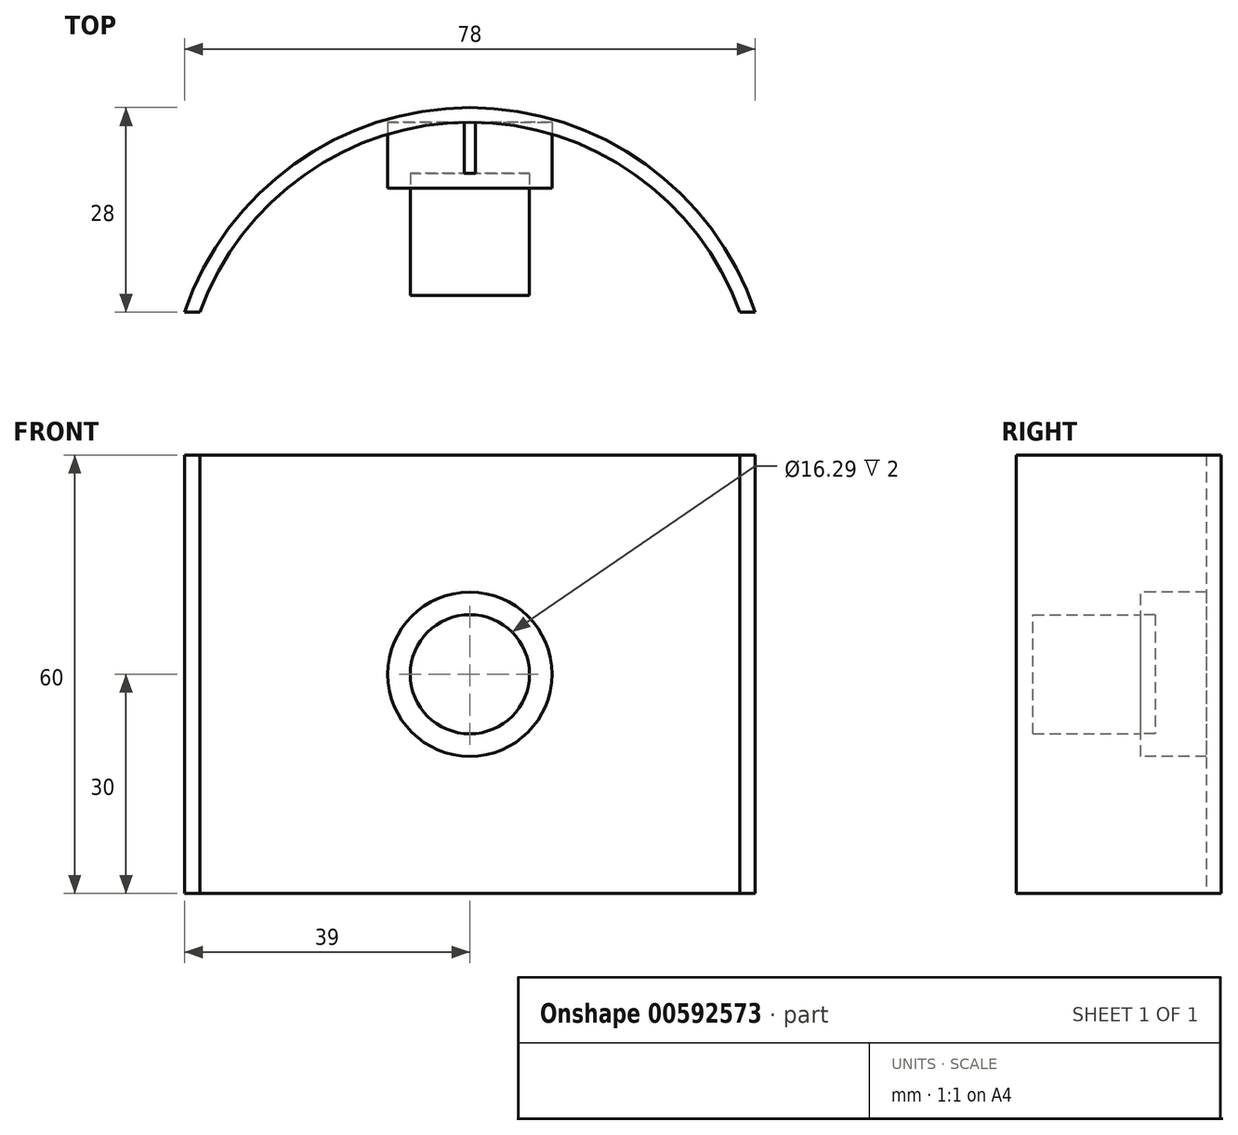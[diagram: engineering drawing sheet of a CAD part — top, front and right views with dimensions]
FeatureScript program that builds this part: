
annotation { "Feature Type Name" : "Feature", "Feature Type Description" : "" }
export const myFeature = defineFeature(function(context is Context, id is Id, definition is map)
    precondition{}
    {
        {
            assignVariable(context, id + "F0", {"name" : "shaft_H1", "anyValue" : 14.7 * mm});
        }
        {
            assignVariable(context, id + "F1", {"name" : "Shaft_H2", "anyValue" : 23.7 * mm});
        }
        {
            assignVariable(context, id + "F2", {"name" : "support", "anyValue" : 16.7 * mm});
        }
        {
            assignVariable(context, id + "F3", {"name" : "HUB_depth1", "anyValue" : getVariable(context, 'support') - getVariable(context, 'shaft_H1')});
        }
        {
            assignVariable(context, id + "F4", {"name" : "support_H1", "anyValue" : getVariable(context, 'Shaft_H2') - getVariable(context, 'shaft_H1') - getVariable(context, 'HUB_depth1')});
        }
        {
            var Q0;
            Q0=qCreatedBy(makeId("Front.planeOp"),FACE);
            var sketch = newSketch(context, id + "F5", { "sketchPlane" : qUnion([Q0])});
            skCircle(sketch, "E0", {"center": v(0, 0) * mm, "radius": 26.88 * mm});
            skCircle(sketch, "E1", {"center": v(0, 0) * mm, "radius": 8.15 * mm, "construction": true});
            skCircle(sketch, "E2", {"center": v(0, 0) * mm, "radius": 11.23 * mm, "construction": true});
            skLineSegment(sketch, "E3", {"start": v(-26.88, 0) * mm, "end": v(26.88, 0) * mm, "construction": true});
            skLineSegment(sketch, "E4", {"start": v(0, -26.88) * mm, "end": v(0, 26.88) * mm, "construction": true});
            skLineSegment(sketch, "E5", {"start": v(0, 26.88) * mm, "end": v(19, 19) * mm, "construction": true});
            skLineSegment(sketch, "E6", {"start": v(19, 19) * mm, "end": v(26.88, 0) * mm, "construction": true});
            skLineSegment(sketch, "E7", {"start": v(26.87, 0) * mm, "end": v(19, -19) * mm, "construction": true});
            skLineSegment(sketch, "E8", {"start": v(19, -19) * mm, "end": v(0, -26.88) * mm, "construction": true});
            skLineSegment(sketch, "E9", {"start": v(0, -26.88) * mm, "end": v(-19, -19) * mm, "construction": true});
            skLineSegment(sketch, "E10", {"start": v(-19, -19) * mm, "end": v(-26.87, 0) * mm, "construction": true});
            skLineSegment(sketch, "E11", {"start": v(-26.88, 0) * mm, "end": v(-19, 19) * mm, "construction": true});
            skLineSegment(sketch, "E12", {"start": v(-19, 19) * mm, "end": v(0, 26.88) * mm, "construction": true});
            skLineSegment(sketch, "E13", {"start": v(-19, 19) * mm, "end": v(19, -19) * mm, "construction": true});
            skLineSegment(sketch, "E14", {"start": v(19, 19) * mm, "end": v(-19, -19) * mm, "construction": true});
            skCircle(sketch, "E15.0", {"center": v(0, 0) * mm, "radius": 28.38 * mm});
            skLineSegment(sketch, "E16", {"start": v(0, -30) * mm, "end": v(0, 30) * mm, "construction": true});
            skLineSegment(sketch, "E17", {"start": v(39, 0) * mm, "end": v(-39, 0) * mm, "construction": true});
            skSolve(sketch);
        }
        {
            var Q0;
            Q0=qCreatedBy(makeId("Front.planeOp"),FACE);
            var sketch = newSketch(context, id + "F6", { "sketchPlane" : qUnion([Q0])});
            skCircle(sketch, "E18", {"center": v(0, 0) * mm, "radius": 8.15 * mm});
            skCircle(sketch, "E19", {"center": v(0, 0) * mm, "radius": 11.23 * mm});
            skSolve(sketch);
        }
        {
            var Q0;
            Q0=makeQuery(id+"F6.imprint","IMPRINT",FACE,{"disambiguationData":[TD([[makeQuery(id+"F6.imprint","IMPRINT",EDGE,{"derivedFrom":sQuery(id+"F6.wireOp",EDGE,"E18")}),1.0]])]});
            extrude(context, id + "F7", {"entities" : qUnion([Q0]), "depth" : getVariable(context, 'shaft_H1'), "offsetDistance" : 25.4 * mm});
        }
        {
            var Q0;
            Q0=makeQuery(id+"F6.imprint","IMPRINT",FACE,{"disambiguationData":[TD([[makeQuery(id+"F6.imprint","IMPRINT",EDGE,{"derivedFrom":sQuery(id+"F6.wireOp",EDGE,"E18")}),-1.0]])]});
            extrude(context, id + "F8", {"entities" : qUnion([Q0]), "oppositeDirection" : true, "depth" : getVariable(context, 'HUB_depth1'), "offsetDistance" : 25.4 * mm});
        }
        {
            var Q0;
            Q0=makeQuery(id+"F8.opExtrude","CAP_FACE",FACE,{"disambiguationData":[OSD([sQuery(id+"F6.wireOp",EDGE,"E18"),sQuery(id+"F6.wireOp",EDGE,"E19")])],"isStart":false});
            var sketch = newSketch(context, id + "F9", { "sketchPlane" : qUnion([Q0])});
            skLineSegment(sketch, "E20.bottom", {"start": v(0.75, 11.2) * mm, "end": v(0, 11.2) * mm});
            skLineSegment(sketch, "E20.top", {"start": v(0.75, 26.88) * mm, "end": v(-0.75, 26.88) * mm});
            skLineSegment(sketch, "E20.left", {"start": v(0.75, 11.2) * mm, "end": v(0.75, 26.88) * mm});
            skLineSegment(sketch, "E20.right", {"start": v(-0.75, 11.2) * mm, "end": v(-0.75, 26.88) * mm});
            skLineSegment(sketch, "E21", {"start": v(0, 11.2) * mm, "end": v(-0.75, 11.2) * mm});
            skLineSegment(sketch, "E22.bottom", {"start": v(-0.75, -11.23) * mm, "end": v(0, -11.23) * mm});
            skLineSegment(sketch, "E22.top", {"start": v(-0.75, -26.9) * mm, "end": v(0.75, -26.9) * mm});
            skLineSegment(sketch, "E22.left", {"start": v(-0.75, -11.23) * mm, "end": v(-0.75, -26.9) * mm});
            skLineSegment(sketch, "E22.right", {"start": v(0.75, -11.23) * mm, "end": v(0.75, -26.9) * mm});
            skLineSegment(sketch, "E23.bottom", {"start": v(-11.23, 0.75) * mm, "end": v(-26.9, 0.75) * mm});
            skLineSegment(sketch, "E23.top", {"start": v(-11.23, -0.75) * mm, "end": v(-26.9, -0.75) * mm});
            skLineSegment(sketch, "E23.left", {"start": v(-11.23, 0.75) * mm, "end": v(-11.23, 0) * mm});
            skLineSegment(sketch, "E23.right", {"start": v(-26.9, 0.75) * mm, "end": v(-26.9, -0.75) * mm});
            skLineSegment(sketch, "E24.bottom", {"start": v(11.23, -0.75) * mm, "end": v(26.9, -0.75) * mm});
            skLineSegment(sketch, "E24.top", {"start": v(11.23, 0.75) * mm, "end": v(26.9, 0.75) * mm});
            skLineSegment(sketch, "E24.left", {"start": v(11.23, -0.75) * mm, "end": v(11.23, 0) * mm});
            skLineSegment(sketch, "E24.right", {"start": v(26.9, -0.75) * mm, "end": v(26.9, 0.75) * mm});
            skLineSegment(sketch, "E25", {"start": v(8.47, 7.41) * mm, "end": v(7.94, 7.94) * mm});
            skLineSegment(sketch, "E26", {"start": v(7.41, 8.47) * mm, "end": v(18.5, 19.55) * mm});
            skLineSegment(sketch, "E27", {"start": v(18.5, 19.55) * mm, "end": v(19.55, 18.5) * mm});
            skLineSegment(sketch, "E28", {"start": v(19.55, 18.5) * mm, "end": v(8.47, 7.41) * mm});
            skLineSegment(sketch, "E29", {"start": v(8.47, -7.41) * mm, "end": v(7.94, -7.94) * mm});
            skLineSegment(sketch, "E30", {"start": v(7.41, -8.47) * mm, "end": v(18.5, -19.55) * mm});
            skLineSegment(sketch, "E31", {"start": v(18.5, -19.55) * mm, "end": v(19.55, -18.5) * mm});
            skLineSegment(sketch, "E32", {"start": v(19.55, -18.5) * mm, "end": v(8.47, -7.41) * mm});
            skLineSegment(sketch, "E33", {"start": v(-7.41, 8.47) * mm, "end": v(-18.5, 19.55) * mm});
            skLineSegment(sketch, "E34", {"start": v(-18.5, 19.55) * mm, "end": v(-19.55, 18.5) * mm});
            skLineSegment(sketch, "E35", {"start": v(-19.55, 18.5) * mm, "end": v(-8.47, 7.41) * mm});
            skLineSegment(sketch, "E36", {"start": v(-8.47, 7.41) * mm, "end": v(-7.94, 7.94) * mm});
            skLineSegment(sketch, "E37", {"start": v(-8.47, -7.41) * mm, "end": v(-7.94, -7.94) * mm});
            skLineSegment(sketch, "E38", {"start": v(-7.41, -8.47) * mm, "end": v(-18.5, -19.55) * mm});
            skLineSegment(sketch, "E39", {"start": v(-18.5, -19.55) * mm, "end": v(-19.55, -18.5) * mm});
            skLineSegment(sketch, "E40", {"start": v(-19.55, -18.5) * mm, "end": v(-8.47, -7.41) * mm});
            skLineSegment(sketch, "E41", {"start": v(-7.94, 7.94) * mm, "end": v(-7.41, 8.47) * mm});
            skLineSegment(sketch, "E42", {"start": v(-7.94, -7.94) * mm, "end": v(-7.41, -8.47) * mm});
            skLineSegment(sketch, "E43", {"start": v(0, -11.23) * mm, "end": v(0.75, -11.23) * mm});
            skLineSegment(sketch, "E44", {"start": v(7.94, -7.94) * mm, "end": v(7.41, -8.47) * mm});
            skLineSegment(sketch, "E45", {"start": v(11.23, 0) * mm, "end": v(11.23, 0.75) * mm});
            skLineSegment(sketch, "E46", {"start": v(7.94, 7.94) * mm, "end": v(7.41, 8.47) * mm});
            skLineSegment(sketch, "E47", {"start": v(-11.23, 0) * mm, "end": v(-11.23, -0.75) * mm});
            skSolve(sketch);
        }
        {
            var Q0;
            {var subQ5=sQuery(id+"F9.wireOp",EDGE,"E20.bottom");Q0=makeQuery(id+"F9.imprint","IMPRINT",FACE,{"disambiguationData":[TD([[makeQuery(id+"F9.imprint","IMPRINT",EDGE,{"derivedFrom":subQ5}),1.0]])]});}
            extrude(context, id + "F10", {"entities" : qUnion([Q0]), "operationType" : NewBodyOperationType.ADD, "depth" : getVariable(context, 'support_H1'), "offsetDistance" : 25.4 * mm});
        }
        {
            var Q0;
            Q0=makeQuery(id+"F9.imprint","IMPRINT",FACE,{"disambiguationData":[TD([[makeQuery(id+"F9.imprint","IMPRINT",EDGE,{"derivedFrom":makeQuery(id+"F8.opExtrude","CAP_EDGE",EDGE,{"disambiguationData":[OSD([sQuery(id+"F6.wireOp",EDGE,"E18")])],"isStart":false})}),-1.0]])]});
            var Q1;
            Q1=makeQuery(id+"F10.opExtrude","CAP_FACE",FACE,{"disambiguationData":[OSD([sQuery(id+"F6.wireOp",EDGE,"E18"),sQuery(id+"F6.wireOp",EDGE,"E19"),sQuery(id+"F9.wireOp",EDGE,"E20.bottom"),sQuery(id+"F9.wireOp",EDGE,"E21")])],"isStart":false});
            extrude(context, id + "F11", {"entities" : qUnion([Q0]), "operationType" : NewBodyOperationType.ADD, "endBound" : BoundingType.UP_TO_SURFACE, "depth" : 25.4 * mm, "endBoundEntityFace" : qUnion([Q1]), "offsetDistance" : 25.4 * mm});
        }
        {
            var Q0;
            Q0=makeQuery(id+"F10.opExtrude","CAP_FACE",FACE,{"disambiguationData":[OSD([sQuery(id+"F6.wireOp",EDGE,"E18"),sQuery(id+"F6.wireOp",EDGE,"E19"),sQuery(id+"F9.wireOp",EDGE,"E20.bottom"),sQuery(id+"F9.wireOp",EDGE,"E21")])],"isStart":false});
            var sketch = newSketch(context, id + "F12", { "sketchPlane" : qUnion([Q0])});
            skLineSegment(sketch, "E48.bottom", {"start": v(-39, -30) * mm, "end": v(39, -30) * mm, "construction": true});
            skLineSegment(sketch, "E48.top", {"start": v(-39, 30) * mm, "end": v(39, 30) * mm, "construction": true});
            skLineSegment(sketch, "E48.left", {"start": v(-39, -30) * mm, "end": v(-39, 30) * mm, "construction": true});
            skLineSegment(sketch, "E48.right", {"start": v(39, -30) * mm, "end": v(39, 30) * mm, "construction": true});
            skPoint(sketch, "E48.middle", {"position": v(0, 0) * mm});
            skSolve(sketch);
        }
        {
            var Q0;
            Q0=qCreatedBy(makeId("Top.planeOp"),FACE);
            var sketch = newSketch(context, id + "F13", { "sketchPlane" : qUnion([Q0])});
            skLineSegment(sketch, "E49.bottom", {"start": v(39, 9) * mm, "end": v(0, 9) * mm, "construction": true});
            skLineSegment(sketch, "E49.top", {"start": v(39, -17) * mm, "end": v(0, -17) * mm, "construction": true});
            skLineSegment(sketch, "E49.left", {"start": v(39, 9) * mm, "end": v(39, -17) * mm, "construction": true});
            skLineSegment(sketch, "E49.right", {"start": v(-39, 9) * mm, "end": v(-39, -17) * mm, "construction": true});
            skLineSegment(sketch, "E50", {"start": v(0, -17) * mm, "end": v(-39, -17) * mm, "construction": true});
            skLineSegment(sketch, "E51", {"start": v(0, 9) * mm, "end": v(-39, 9) * mm, "construction": true});
            skLineSegment(sketch, "E52.0", {"start": v(39, 11) * mm, "end": v(0, 11) * mm, "construction": true});
            skArc(sketch, "E53", {"start": v(39, -17) * mm, "mid": v(0, 11) * mm, "end": v(-39, -17) * mm});
            skArc(sketch, "E54.0", {"start": v(36.88, -17) * mm, "mid": v(0, 9) * mm, "end": v(-36.88, -17) * mm});
            skLineSegment(sketch, "E55", {"start": v(36.88, -17) * mm, "end": v(39, -17) * mm});
            skLineSegment(sketch, "E56", {"start": v(-39, -17) * mm, "end": v(-36.88, -17) * mm});
            skSolve(sketch);
        }
        {
            var Q0;
            Q0=makeQuery(id+"F13.imprint","IMPRINT",FACE,{"disambiguationData":[TD([[makeQuery(id+"F13.imprint","IMPRINT",EDGE,{"derivedFrom":sQuery(id+"F13.wireOp",EDGE,"E53")}),1.0]])]});
            extrude(context, id + "F14", {"entities" : qUnion([Q0]), "endBound" : BoundingType.SYMMETRIC, "depth" : 60 * mm, "offsetDistance" : 25.4 * mm});
        }
    });
